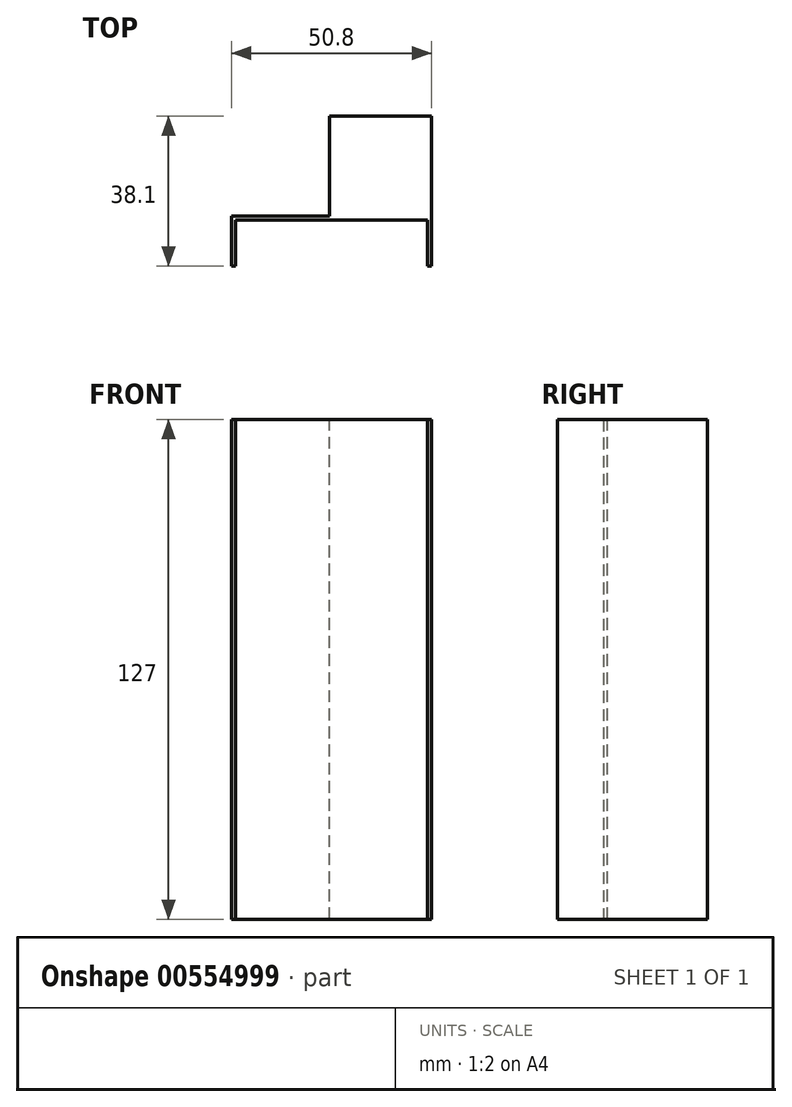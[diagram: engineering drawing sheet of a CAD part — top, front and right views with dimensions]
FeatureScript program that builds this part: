
annotation { "Feature Type Name" : "Feature", "Feature Type Description" : "" }
export const myFeature = defineFeature(function(context is Context, id is Id, definition is map)
    precondition{}
    {
        {
            var Q0;
            Q0=qCreatedBy(makeId("Top.planeOp"),FACE);
            var sketch = newSketch(context, id + "F0", { "sketchPlane" : qUnion([Q0])});
            skLineSegment(sketch, "E0.bottom", {"start": v(25.4, 6.35) * mm, "end": v(-25.4, 6.35) * mm});
            skLineSegment(sketch, "E0.top", {"start": v(25.4, -6.35) * mm, "end": v(-25.4, -6.35) * mm});
            skLineSegment(sketch, "E0.left", {"start": v(25.4, 6.35) * mm, "end": v(25.4, -6.35) * mm});
            skLineSegment(sketch, "E0.right", {"start": v(-25.4, 6.35) * mm, "end": v(-25.4, -6.35) * mm});
            skPoint(sketch, "E0.middle", {"position": v(0, 0) * mm});
            skSolve(sketch);
        }
        {
            var Q0;
            Q0=makeQuery(id+"F0.imprint","IMPRINT",FACE,{"disambiguationData":[TD([[makeQuery(id+"F0.imprint","IMPRINT",EDGE,{"derivedFrom":sQuery(id+"F0.wireOp",EDGE,"E0.bottom")}),1.0]])]});
            extrude(context, id + "F1", {"entities" : qUnion([Q0]), "depth" : 127 * mm, "offsetDistance" : 25.4 * mm});
        }
        {
            var Q0;
            Q0=makeQuery(id+"F1.opExtrude","CAP_FACE",FACE,{"disambiguationData":[OSD([sQuery(id+"F0.wireOp",EDGE,"E0.bottom"),sQuery(id+"F0.wireOp",EDGE,"E0.top"),sQuery(id+"F0.wireOp",EDGE,"E0.left"),sQuery(id+"F0.wireOp",EDGE,"E0.right")])],"isStart":false});
            var Q1;
            Q1=makeQuery(id+"F1.opExtrude","SWEPT_FACE",FACE,{"disambiguationData":[OSD([sQuery(id+"F0.wireOp",EDGE,"E0.top")])]});
            var Q2;
            Q2=makeQuery(id+"F1.opExtrude","CAP_FACE",FACE,{"disambiguationData":[OSD([sQuery(id+"F0.wireOp",EDGE,"E0.bottom"),sQuery(id+"F0.wireOp",EDGE,"E0.top"),sQuery(id+"F0.wireOp",EDGE,"E0.left"),sQuery(id+"F0.wireOp",EDGE,"E0.right")])],"isStart":true});
            shell(context, id + "F2", {"entities" : qUnion([Q0, Q1, Q2]), "thickness" : 1 * mm});
        }
        {
            var Q0;
            Q0=makeQuery(id+"F1.opExtrude","SWEPT_FACE",FACE,{"disambiguationData":[OSD([sQuery(id+"F0.wireOp",EDGE,"E0.bottom")])]});
            var sketch = newSketch(context, id + "F3", { "sketchPlane" : qUnion([Q0])});
            skLineSegment(sketch, "E1.bottom", {"start": v(25.4, 127) * mm, "end": v(-25.4, 127) * mm});
            skLineSegment(sketch, "E1.top", {"start": v(25.4, 0) * mm, "end": v(-25.4, 0) * mm});
            skLineSegment(sketch, "E1.left", {"start": v(25.4, 127) * mm, "end": v(25.4, 0) * mm});
            skLineSegment(sketch, "E1.right", {"start": v(-25.4, 127) * mm, "end": v(-25.4, 0) * mm});
            skSolve(sketch);
        }
        {
            var Q0;
            Q0 = qSketchRegion(id + "F3", true);
            extrude(context, id + "F4", {"entities" : qUnion([Q0]), "operationType" : NewBodyOperationType.ADD, "depth" : 25.4 * mm, "offsetDistance" : 25.4 * mm});
        }
        {
            var Q0;
            Q0=makeQuery(id+"F4.boolean.opBoolean","MERGE",FACE,{"derivedFrom":[makeQuery(id+"F1.opExtrude","CAP_FACE",FACE,{"disambiguationData":[OSD([sQuery(id+"F0.wireOp",EDGE,"E0.bottom"),sQuery(id+"F0.wireOp",EDGE,"E0.top"),sQuery(id+"F0.wireOp",EDGE,"E0.left"),sQuery(id+"F0.wireOp",EDGE,"E0.right")])],"isStart":false}),makeQuery(id+"F4.opExtrude","SWEPT_FACE",FACE,{"disambiguationData":[OSD([sQuery(id+"F3.wireOp",EDGE,"E1.bottom")])]})]});
            var sketch = newSketch(context, id + "F5", { "sketchPlane" : qUnion([Q0])});
            skLineSegment(sketch, "E2.bottom", {"start": v(-25.4, 6.35) * mm, "end": v(-0.5, 6.35) * mm});
            skLineSegment(sketch, "E2.top", {"start": v(-25.4, 31.75) * mm, "end": v(-0.5, 31.75) * mm});
            skLineSegment(sketch, "E2.left", {"start": v(-25.4, 6.35) * mm, "end": v(-25.4, 31.75) * mm});
            skLineSegment(sketch, "E2.right", {"start": v(-0.5, 6.35) * mm, "end": v(-0.5, 31.75) * mm});
            skSolve(sketch);
        }
        {
            var Q0;
            Q0 = qSketchRegion(id + "F5", true);
            extrude(context, id + "F6", {"entities" : qUnion([Q0]), "operationType" : NewBodyOperationType.REMOVE, "oppositeDirection" : true, "depth" : 127 * mm, "offsetDistance" : 25.4 * mm});
        }
    });
